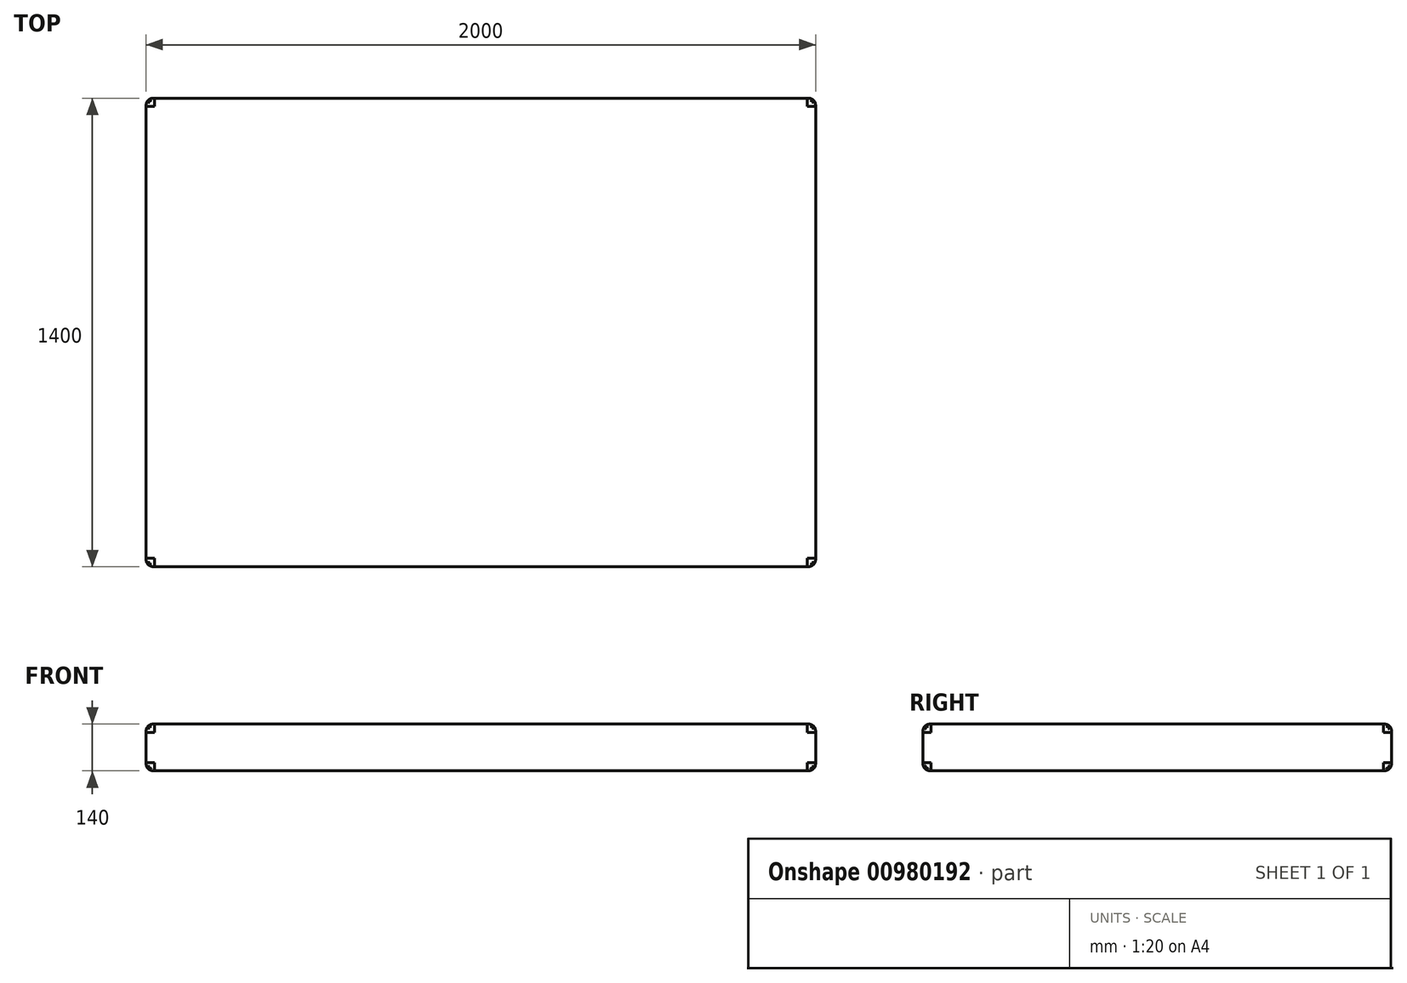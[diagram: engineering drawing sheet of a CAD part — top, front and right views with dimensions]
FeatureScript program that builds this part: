
annotation { "Feature Type Name" : "Feature", "Feature Type Description" : "" }
export const myFeature = defineFeature(function(context is Context, id is Id, definition is map)
    precondition{}
    {
        {
            var Q0;
            Q0=qCreatedBy(makeId("Top.planeOp"),FACE);
            var sketch = newSketch(context, id + "F0", { "sketchPlane" : qUnion([Q0])});
            skLineSegment(sketch, "E0.bottom", {"start": v(1000, 700) * mm, "end": v(-1000, 700) * mm});
            skLineSegment(sketch, "E0.top", {"start": v(1000, -700) * mm, "end": v(-1000, -700) * mm});
            skLineSegment(sketch, "E0.left", {"start": v(1000, 700) * mm, "end": v(1000, -700) * mm});
            skLineSegment(sketch, "E0.right", {"start": v(-1000, 700) * mm, "end": v(-1000, -700) * mm});
            skPoint(sketch, "E0.middle", {"position": v(0, 0) * mm});
            skSolve(sketch);
        }
        {
            var Q0;
            Q0=makeQuery(id+"F0.imprint","IMPRINT",FACE,{"disambiguationData":[TD([[makeQuery(id+"F0.imprint","IMPRINT",EDGE,{"derivedFrom":sQuery(id+"F0.wireOp",EDGE,"E0.bottom")}),1.0]])]});
            extrude(context, id + "F1", {"entities" : qUnion([Q0]), "depth" : 140 * mm, "offsetDistance" : 25 * mm});
        }
        {
            var Q0;
            Q0=makeQuery(id+"F1.opExtrude","CAP_EDGE",EDGE,{"disambiguationData":[OSD([sQuery(id+"F0.wireOp",EDGE,"E0.top")])],"isStart":false});
            var Q1;
            Q1=makeQuery(id+"F1.opExtrude","CAP_EDGE",EDGE,{"disambiguationData":[OSD([sQuery(id+"F0.wireOp",EDGE,"E0.right")])],"isStart":false});
            var Q2;
            Q2=makeQuery(id+"F1.opExtrude","CAP_EDGE",EDGE,{"disambiguationData":[OSD([sQuery(id+"F0.wireOp",EDGE,"E0.bottom")])],"isStart":false});
            var Q3;
            Q3=makeQuery(id+"F1.opExtrude","CAP_EDGE",EDGE,{"disambiguationData":[OSD([sQuery(id+"F0.wireOp",EDGE,"E0.left")])],"isStart":false});
            var Q4;
            Q4=makeQuery(id+"F1.opExtrude","SWEPT_FACE",FACE,{"disambiguationData":[OSD([sQuery(id+"F0.wireOp",EDGE,"E0.top")])]});
            var Q5;
            Q5=makeQuery(id+"F1.opExtrude","CAP_EDGE",EDGE,{"disambiguationData":[OSD([sQuery(id+"F0.wireOp",EDGE,"E0.right")])],"isStart":true});
            var Q6;
            Q6=makeQuery(id+"F1.opExtrude","CAP_EDGE",EDGE,{"disambiguationData":[OSD([sQuery(id+"F0.wireOp",EDGE,"E0.bottom")])],"isStart":true});
            var Q7;
            Q7=makeQuery(id+"F1.opExtrude","SWEPT_EDGE",EDGE,{"disambiguationData":[OSD([sQuery(id+"F0.wireOp",EDGE,"E0.bottom"),sQuery(id+"F0.wireOp",EDGE,"E0.right")])]});
            var Q8;
            Q8=makeQuery(id+"F1.opExtrude","SWEPT_EDGE",EDGE,{"disambiguationData":[OSD([sQuery(id+"F0.wireOp",EDGE,"E0.bottom"),sQuery(id+"F0.wireOp",EDGE,"E0.left")])]});
            var Q9;
            Q9=makeQuery(id+"F1.opExtrude","CAP_EDGE",EDGE,{"disambiguationData":[OSD([sQuery(id+"F0.wireOp",EDGE,"E0.left")])],"isStart":true});
            fillet(context, id + "F2", {"entities" : qUnion([Q0, Q1, Q2, Q3, Q4, Q5, Q6, Q7, Q8, Q9]), "radius" : 25 * mm, "tangentPropagation" : true, "rho" : 0.5, "crossSection" : FilletCrossSection.CONIC, "allowEdgeOverflow" : false});
        }
    });
